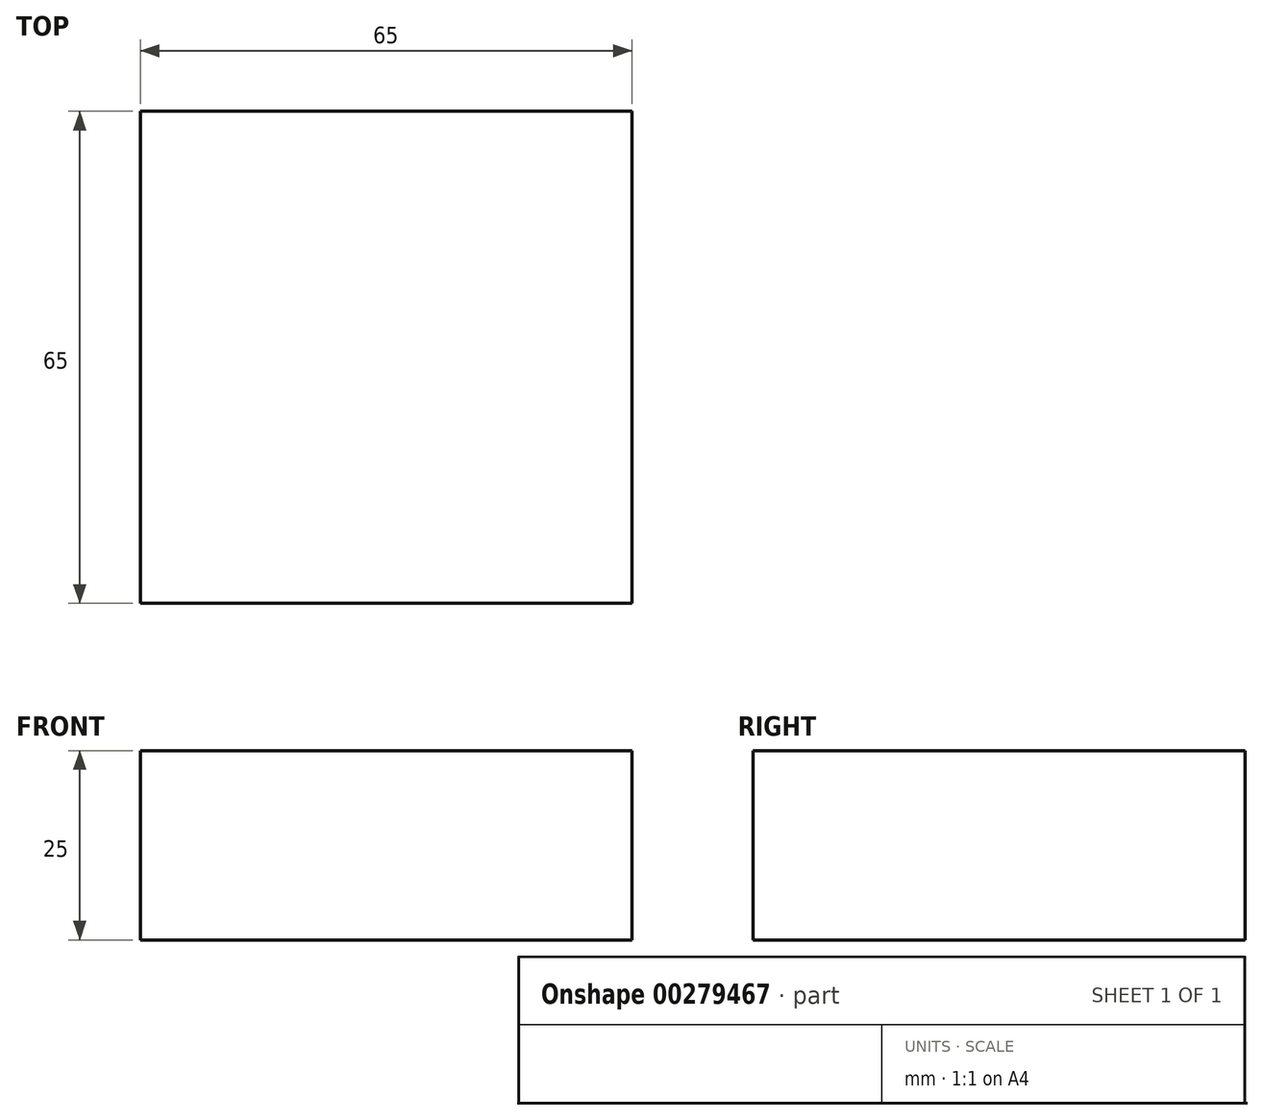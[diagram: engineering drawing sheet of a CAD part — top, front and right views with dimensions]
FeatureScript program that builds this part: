
annotation { "Feature Type Name" : "Feature", "Feature Type Description" : "" }
export const myFeature = defineFeature(function(context is Context, id is Id, definition is map)
    precondition{}
    {
        {
            var Q0;
            Q0=qCreatedBy(makeId("Top.planeOp"),FACE);
            var sketch = newSketch(context, id + "F0", { "sketchPlane" : qUnion([Q0])});
            skLineSegment(sketch, "E0.bottom", {"start": v(-56, 50.64) * mm, "end": v(9, 50.64) * mm});
            skLineSegment(sketch, "E0.top", {"start": v(-56, -14.36) * mm, "end": v(9, -14.36) * mm});
            skLineSegment(sketch, "E0.left", {"start": v(-56, 50.64) * mm, "end": v(-56, -14.36) * mm});
            skLineSegment(sketch, "E0.right", {"start": v(9, 50.64) * mm, "end": v(9, -14.36) * mm});
            skSolve(sketch);
        }
        {
            var Q0;
            Q0 = qSketchRegion(id + "F0", true);
            extrude(context, id + "F1", {"entities" : qUnion([Q0]), "depth" : 25 * mm});
        }
    });
